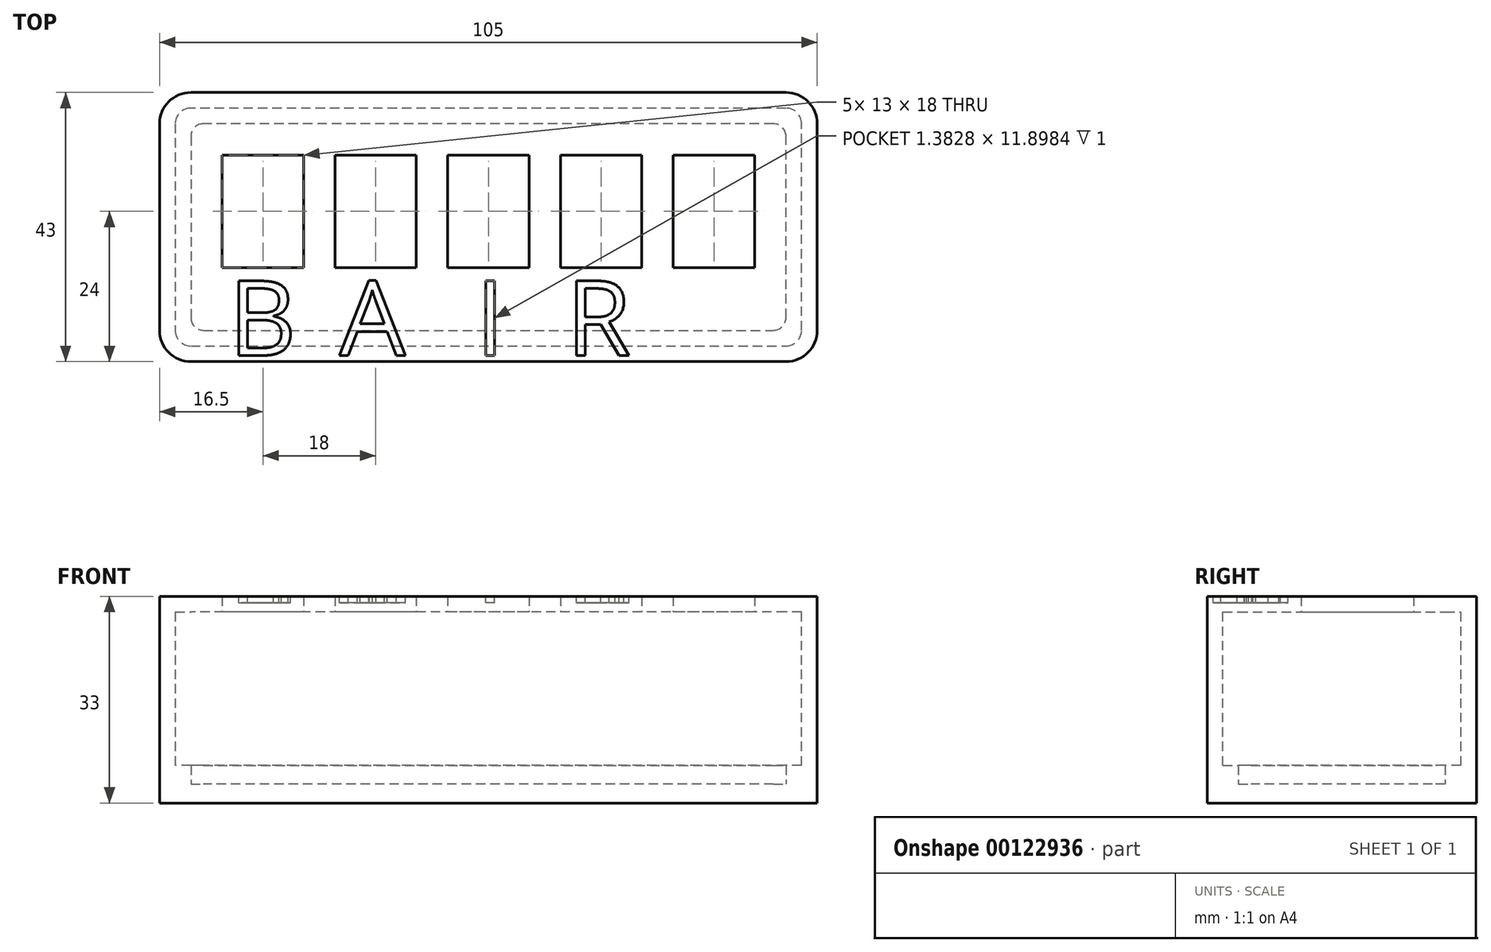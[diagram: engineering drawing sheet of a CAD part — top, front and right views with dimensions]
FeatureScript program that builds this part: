
annotation { "Feature Type Name" : "Feature", "Feature Type Description" : "" }
export const myFeature = defineFeature(function(context is Context, id is Id, definition is map)
    precondition{}
    {
        {
            var Q0;
            Q0=qCreatedBy(makeId("Top.planeOp"),FACE);
            var sketch = newSketch(context, id + "F0", { "sketchPlane" : qUnion([Q0])});
            skLineSegment(sketch, "E0.bottom", {"start": v(-42.5, 33) * mm, "end": v(-29.5, 33) * mm});
            skLineSegment(sketch, "E0.top", {"start": v(-42.5, 15) * mm, "end": v(-29.5, 15) * mm});
            skLineSegment(sketch, "E0.left", {"start": v(-42.5, 33) * mm, "end": v(-42.5, 15) * mm});
            skLineSegment(sketch, "E0.right", {"start": v(-29.5, 33) * mm, "end": v(-29.5, 15) * mm});
            skLineSegment(sketch, "E1.1.0.0", {"start": v(-24.5, 33) * mm, "end": v(-24.5, 15) * mm});
            skLineSegment(sketch, "E1.1.0.1", {"start": v(-24.5, 33) * mm, "end": v(-11.5, 33) * mm});
            skLineSegment(sketch, "E1.1.0.2", {"start": v(-24.5, 15) * mm, "end": v(-11.5, 15) * mm});
            skLineSegment(sketch, "E1.1.0.3", {"start": v(-11.5, 33) * mm, "end": v(-11.5, 15) * mm});
            skLineSegment(sketch, "E1.2.0.0", {"start": v(-6.5, 33) * mm, "end": v(-6.5, 15) * mm});
            skLineSegment(sketch, "E1.2.0.1", {"start": v(-6.5, 33) * mm, "end": v(6.5, 33) * mm});
            skLineSegment(sketch, "E1.2.0.2", {"start": v(-6.5, 15) * mm, "end": v(6.5, 15) * mm});
            skLineSegment(sketch, "E1.2.0.3", {"start": v(6.5, 33) * mm, "end": v(6.5, 15) * mm});
            skLineSegment(sketch, "E1.3.0.0", {"start": v(11.5, 33) * mm, "end": v(11.5, 15) * mm});
            skLineSegment(sketch, "E1.3.0.1", {"start": v(11.5, 33) * mm, "end": v(24.5, 33) * mm});
            skLineSegment(sketch, "E1.3.0.2", {"start": v(11.5, 15) * mm, "end": v(24.5, 15) * mm});
            skLineSegment(sketch, "E1.3.0.3", {"start": v(24.5, 33) * mm, "end": v(24.5, 15) * mm});
            skLineSegment(sketch, "E1.4.0.0", {"start": v(29.5, 33) * mm, "end": v(29.5, 15) * mm});
            skLineSegment(sketch, "E1.4.0.1", {"start": v(29.5, 33) * mm, "end": v(42.5, 33) * mm});
            skLineSegment(sketch, "E1.4.0.2", {"start": v(29.5, 15) * mm, "end": v(42.5, 15) * mm});
            skLineSegment(sketch, "E1.4.0.3", {"start": v(42.5, 33) * mm, "end": v(42.5, 15) * mm});
            skLineSegment(sketch, "E1.direction1", {"start": v(-42.5, 15) * mm, "end": v(-24.5, 15) * mm, "construction": true});
            skLineSegment(sketch, "E2", {"start": v(-52.5, 43) * mm, "end": v(-52.5, 0) * mm});
            skLineSegment(sketch, "E3", {"start": v(-52.5, 0) * mm, "end": v(52.5, 0) * mm});
            skLineSegment(sketch, "E4", {"start": v(52.5, 0) * mm, "end": v(52.5, 43) * mm});
            skLineSegment(sketch, "E5", {"start": v(52.5, 43) * mm, "end": v(-52.5, 43) * mm});
            skSolve(sketch);
        }
        {
            var Q0;
            Q0=makeQuery(id+"F0.imprint","IMPRINT",FACE,{"disambiguationData":[TD([[makeQuery(id+"F0.imprint","IMPRINT",EDGE,{"derivedFrom":sQuery(id+"F0.wireOp",EDGE,"E0.bottom")}),1.0]])]});
            var Q1;
            Q1=makeQuery(id+"F0.imprint","IMPRINT",FACE,{"disambiguationData":[TD([[makeQuery(id+"F0.imprint","IMPRINT",EDGE,{"derivedFrom":sQuery(id+"F0.wireOp",EDGE,"E0.bottom")}),-1.0]])]});
            var Q2;
            Q2=makeQuery(id+"F0.imprint","IMPRINT",FACE,{"disambiguationData":[TD([[makeQuery(id+"F0.imprint","IMPRINT",EDGE,{"derivedFrom":sQuery(id+"F0.wireOp",EDGE,"E1.1.0.0")}),1.0]])]});
            var Q3;
            Q3=makeQuery(id+"F0.imprint","IMPRINT",FACE,{"disambiguationData":[TD([[makeQuery(id+"F0.imprint","IMPRINT",EDGE,{"derivedFrom":sQuery(id+"F0.wireOp",EDGE,"E1.2.0.0")}),1.0]])]});
            var Q4;
            Q4=makeQuery(id+"F0.imprint","IMPRINT",FACE,{"disambiguationData":[TD([[makeQuery(id+"F0.imprint","IMPRINT",EDGE,{"derivedFrom":sQuery(id+"F0.wireOp",EDGE,"E1.3.0.0")}),1.0]])]});
            var Q5;
            Q5=makeQuery(id+"F0.imprint","IMPRINT",FACE,{"disambiguationData":[TD([[makeQuery(id+"F0.imprint","IMPRINT",EDGE,{"derivedFrom":sQuery(id+"F0.wireOp",EDGE,"E1.4.0.0")}),1.0]])]});
            extrude(context, id + "F1", {"entities" : qUnion([Q0, Q1, Q2, Q3, Q4, Q5]), "depth" : 30 * mm});
        }
        {
            var Q0;
            Q0=makeQuery(id+"F1.opExtrude","SWEPT_EDGE",EDGE,{"disambiguationData":[OSD([sQuery(id+"F0.wireOp",EDGE,"E2"),sQuery(id+"F0.wireOp",EDGE,"E3")])]});
            var Q1;
            Q1=makeQuery(id+"F1.opExtrude","SWEPT_EDGE",EDGE,{"disambiguationData":[OSD([sQuery(id+"F0.wireOp",EDGE,"E3"),sQuery(id+"F0.wireOp",EDGE,"E4")])]});
            var Q2;
            Q2=makeQuery(id+"F1.opExtrude","SWEPT_EDGE",EDGE,{"disambiguationData":[OSD([sQuery(id+"F0.wireOp",EDGE,"E4"),sQuery(id+"F0.wireOp",EDGE,"E5")])]});
            var Q3;
            Q3=makeQuery(id+"F1.opExtrude","SWEPT_EDGE",EDGE,{"disambiguationData":[OSD([sQuery(id+"F0.wireOp",EDGE,"E2"),sQuery(id+"F0.wireOp",EDGE,"E5")])]});
            fillet(context, id + "F2", {"entities" : qUnion([Q0, Q1, Q2, Q3]), "radius" : 5 * mm, "tangentPropagation" : true, "allowEdgeOverflow" : false});
        }
        {
            var Q0;
            Q0=makeQuery(id+"F1.opExtrude","CAP_FACE",FACE,{"disambiguationData":[OSD([sQuery(id+"F0.wireOp",EDGE,"E2"),sQuery(id+"F0.wireOp",EDGE,"E3"),sQuery(id+"F0.wireOp",EDGE,"E4"),sQuery(id+"F0.wireOp",EDGE,"E5")])],"isStart":true});
            shell(context, id + "F3", {"entities" : qUnion([Q0]), "thickness" : 2.5 * mm});
        }
        {
            var Q0;
            Q0=makeQuery(id+"F0.imprint","IMPRINT",FACE,{"disambiguationData":[TD([[makeQuery(id+"F0.imprint","IMPRINT",EDGE,{"derivedFrom":sQuery(id+"F0.wireOp",EDGE,"E0.bottom")}),-1.0]])]});
            var Q1;
            Q1=makeQuery(id+"F0.imprint","IMPRINT",FACE,{"disambiguationData":[TD([[makeQuery(id+"F0.imprint","IMPRINT",EDGE,{"derivedFrom":sQuery(id+"F0.wireOp",EDGE,"E1.1.0.0")}),1.0]])]});
            var Q2;
            Q2=makeQuery(id+"F0.imprint","IMPRINT",FACE,{"disambiguationData":[TD([[makeQuery(id+"F0.imprint","IMPRINT",EDGE,{"derivedFrom":sQuery(id+"F0.wireOp",EDGE,"E1.2.0.0")}),1.0]])]});
            var Q3;
            Q3=makeQuery(id+"F0.imprint","IMPRINT",FACE,{"disambiguationData":[TD([[makeQuery(id+"F0.imprint","IMPRINT",EDGE,{"derivedFrom":sQuery(id+"F0.wireOp",EDGE,"E1.3.0.0")}),1.0]])]});
            var Q4;
            Q4=makeQuery(id+"F0.imprint","IMPRINT",FACE,{"disambiguationData":[TD([[makeQuery(id+"F0.imprint","IMPRINT",EDGE,{"derivedFrom":sQuery(id+"F0.wireOp",EDGE,"E1.4.0.0")}),1.0]])]});
            var Q5;
            Q5=makeQuery(id+"F1.opExtrude","CAP_FACE",FACE,{"disambiguationData":[OSD([sQuery(id+"F0.wireOp",EDGE,"E2"),sQuery(id+"F0.wireOp",EDGE,"E3"),sQuery(id+"F0.wireOp",EDGE,"E4"),sQuery(id+"F0.wireOp",EDGE,"E5")])],"isStart":false});
            extrude(context, id + "F4", {"entities" : qUnion([Q0, Q1, Q2, Q3, Q4]), "operationType" : NewBodyOperationType.REMOVE, "endBound" : BoundingType.UP_TO_SURFACE, "endBoundEntityFace" : qUnion([Q5]), "depth" : 25 * mm});
        }
        {
            var Q0;
            Q0=makeQuery(id+"F1.opExtrude","CAP_FACE",FACE,{"disambiguationData":[OSD([sQuery(id+"F0.wireOp",EDGE,"E2"),sQuery(id+"F0.wireOp",EDGE,"E3"),sQuery(id+"F0.wireOp",EDGE,"E4"),sQuery(id+"F0.wireOp",EDGE,"E5")])],"isStart":false});
            var sketch = newSketch(context, id + "F5", { "sketchPlane" : qUnion([Q0])});
            skLineSegment(sketch, "E6.0.0", {"start": v(-42.5, 33) * mm, "end": v(-42.5, 15) * mm});
            skLineSegment(sketch, "E6.0.1", {"start": v(-42.5, 15) * mm, "end": v(-29.5, 15) * mm});
            skLineSegment(sketch, "E6.0.2", {"start": v(-29.5, 15) * mm, "end": v(-29.5, 33) * mm});
            skLineSegment(sketch, "E6.0.3", {"start": v(-29.5, 33) * mm, "end": v(-42.5, 33) * mm});
            skLineSegment(sketch, "E7.0.0", {"start": v(-11.5, 15) * mm, "end": v(-11.5, 33) * mm});
            skLineSegment(sketch, "E7.0.1", {"start": v(-11.5, 33) * mm, "end": v(-24.5, 33) * mm});
            skLineSegment(sketch, "E7.0.2", {"start": v(-24.5, 33) * mm, "end": v(-24.5, 15) * mm});
            skLineSegment(sketch, "E7.0.3", {"start": v(-24.5, 15) * mm, "end": v(-11.5, 15) * mm});
            skLineSegment(sketch, "E8.0.0", {"start": v(6.5, 15) * mm, "end": v(6.5, 33) * mm});
            skLineSegment(sketch, "E8.0.1", {"start": v(6.5, 33) * mm, "end": v(-6.5, 33) * mm});
            skLineSegment(sketch, "E8.0.2", {"start": v(-6.5, 33) * mm, "end": v(-6.5, 15) * mm});
            skLineSegment(sketch, "E8.0.3", {"start": v(-6.5, 15) * mm, "end": v(6.5, 15) * mm});
            skLineSegment(sketch, "E9.0.0", {"start": v(24.5, 15) * mm, "end": v(24.5, 33) * mm});
            skLineSegment(sketch, "E9.0.1", {"start": v(24.5, 33) * mm, "end": v(11.5, 33) * mm});
            skLineSegment(sketch, "E9.0.2", {"start": v(11.5, 33) * mm, "end": v(11.5, 15) * mm});
            skLineSegment(sketch, "E9.0.3", {"start": v(11.5, 15) * mm, "end": v(24.5, 15) * mm});
            skLineSegment(sketch, "E10.0.0", {"start": v(42.5, 15) * mm, "end": v(42.5, 33) * mm});
            skLineSegment(sketch, "E10.0.1", {"start": v(42.5, 33) * mm, "end": v(29.5, 33) * mm});
            skLineSegment(sketch, "E10.0.2", {"start": v(29.5, 33) * mm, "end": v(29.5, 15) * mm});
            skLineSegment(sketch, "E10.0.3", {"start": v(29.5, 15) * mm, "end": v(42.5, 15) * mm});
            skLineSegment(sketch, "E11.0", {"start": v(-47.5, 0) * mm, "end": v(47.5, 0) * mm});
            skText(sketch, "E12", { "text": "B", "fontName": "OpenSans-Regular.ttf"});
            skPoint(sketch, "E13", {"position": v(-36, 15) * mm});
            skLineSegment(sketch, "E14", {"start": v(-36, 15) * mm, "end": v(-36, 0) * mm, "construction": true});
            skLineSegment(sketch, "E15", {"start": v(-18, 15) * mm, "end": v(-18, 0) * mm, "construction": true});
            skLineSegment(sketch, "E16", {"start": v(0, 15) * mm, "end": v(0, 0) * mm, "construction": true});
            skLineSegment(sketch, "E17", {"start": v(18, 15) * mm, "end": v(18, 0) * mm, "construction": true});
            skLineSegment(sketch, "E18", {"start": v(36, 15) * mm, "end": v(36, 0) * mm, "construction": true});
            skLineSegment(sketch, "E19", {"start": v(-36, 13) * mm, "end": v(-18, 13) * mm, "construction": true});
            skText(sketch, "E20", { "text": "A", "fontName": "OpenSans-Regular.ttf"});
            skLineSegment(sketch, "E21", {"start": v(-18, 13) * mm, "end": v(0, 13) * mm, "construction": true});
            skLineSegment(sketch, "E22", {"start": v(0, 13) * mm, "end": v(18, 13) * mm, "construction": true});
            skLineSegment(sketch, "E23", {"start": v(18, 13) * mm, "end": v(36, 13) * mm, "construction": true});
            skText(sketch, "E24", { "text": "I", "fontName": "OpenSans-Regular.ttf"});
            skText(sketch, "E25", { "text": "R", "fontName": "OpenSans-Regular.ttf"});
            const initialGuessF5  = {"E12": [-0.04148, 0.001, 1, 0, 0.012], "E20": [-0.02381, 0.001, 1, 0, 0.012], "E24": [-0.00205, 0.001, 1, 0, 0.012], "E25": [0.01245, 0.001, 1, 0, 0.012]};
            skSetInitialGuess(sketch, initialGuessF5);
            skSolve(sketch);
        }
        {
            var Q0;
            Q0=makeQuery(id+"F5.imprint","IMPRINT",FACE,{"disambiguationData":[TD([[makeQuery(id+"F5.imprint","IMPRINT",EDGE,{"derivedFrom":sQuery(id+"F5.wireOp",EDGE,"E12.sketch_text.stroke-0")}),-1.0]])]});
            var Q1;
            Q1=makeQuery(id+"F5.imprint","IMPRINT",FACE,{"disambiguationData":[TD([[makeQuery(id+"F5.imprint","IMPRINT",EDGE,{"derivedFrom":sQuery(id+"F5.wireOp",EDGE,"E20.sketch_text.stroke-0")}),-1.0]])]});
            var Q2;
            Q2=makeQuery(id+"F5.imprint","IMPRINT",FACE,{"disambiguationData":[TD([[makeQuery(id+"F5.imprint","IMPRINT",EDGE,{"derivedFrom":sQuery(id+"F5.wireOp",EDGE,"E24.sketch_text.stroke-0")}),-1.0]])]});
            var Q3;
            Q3=makeQuery(id+"F5.imprint","IMPRINT",FACE,{"disambiguationData":[TD([[makeQuery(id+"F5.imprint","IMPRINT",EDGE,{"derivedFrom":sQuery(id+"F5.wireOp",EDGE,"E25.sketch_text.stroke-0")}),-1.0]])]});
            extrude(context, id + "F6", {"entities" : qUnion([Q0, Q1, Q2, Q3]), "operationType" : NewBodyOperationType.REMOVE, "oppositeDirection" : true, "depth" : 1 * mm});
        }
        {
            var Q0;
            Q0=makeQuery(id+"F1.opExtrude","CAP_FACE",FACE,{"disambiguationData":[OSD([sQuery(id+"F0.wireOp",EDGE,"E2"),sQuery(id+"F0.wireOp",EDGE,"E3"),sQuery(id+"F0.wireOp",EDGE,"E4"),sQuery(id+"F0.wireOp",EDGE,"E5")])],"isStart":true});
            var sketch = newSketch(context, id + "F7", { "sketchPlane" : qUnion([Q0])});
            skLineSegment(sketch, "E26.0.0", {"start": v(-47.5, -43) * mm, "end": v(47.5, -43) * mm});
            skArc(sketch, "E26.0.1", {"start": v(47.5, -43) * mm, "mid": v(51.04, -41.54) * mm, "end": v(52.5, -38) * mm});
            skLineSegment(sketch, "E26.0.2", {"start": v(52.5, -38) * mm, "end": v(52.5, -5) * mm});
            skArc(sketch, "E26.0.3", {"start": v(52.5, -5) * mm, "mid": v(51.04, -1.46) * mm, "end": v(47.5, 0) * mm});
            skLineSegment(sketch, "E26.0.4", {"start": v(47.5, 0) * mm, "end": v(-47.5, 0) * mm});
            skArc(sketch, "E26.0.5", {"start": v(-47.5, 0) * mm, "mid": v(-51.04, -1.46) * mm, "end": v(-52.5, -5) * mm});
            skLineSegment(sketch, "E26.0.6", {"start": v(-52.5, -5) * mm, "end": v(-52.5, -38) * mm});
            skArc(sketch, "E26.0.7", {"start": v(-52.5, -38) * mm, "mid": v(-51.04, -41.54) * mm, "end": v(-47.5, -43) * mm});
            skLineSegment(sketch, "E27.0", {"start": v(-47.5, -2.5) * mm, "end": v(47.5, -2.5) * mm});
            skArc(sketch, "E28.0", {"start": v(50, -5) * mm, "mid": v(49.27, -3.23) * mm, "end": v(47.5, -2.5) * mm});
            skLineSegment(sketch, "E29.0", {"start": v(50, -5) * mm, "end": v(50, -38) * mm});
            skArc(sketch, "E30.0", {"start": v(47.5, -40.5) * mm, "mid": v(49.27, -39.77) * mm, "end": v(50, -38) * mm});
            skLineSegment(sketch, "E31.0", {"start": v(47.5, -40.5) * mm, "end": v(-47.5, -40.5) * mm});
            skArc(sketch, "E32.0", {"start": v(-50, -38) * mm, "mid": v(-49.27, -39.77) * mm, "end": v(-47.5, -40.5) * mm});
            skLineSegment(sketch, "E33.0", {"start": v(-50, -38) * mm, "end": v(-50, -5) * mm});
            skArc(sketch, "E34.0", {"start": v(-47.5, -2.5) * mm, "mid": v(-49.27, -3.23) * mm, "end": v(-50, -5) * mm});
            skLineSegment(sketch, "E35.0", {"start": v(45.5, -38) * mm, "end": v(-45.5, -38) * mm});
            skLineSegment(sketch, "E35.1", {"start": v(47.5, -7) * mm, "end": v(47.5, -36) * mm});
            skLineSegment(sketch, "E35.2", {"start": v(-45.5, -5) * mm, "end": v(45.5, -5) * mm});
            skLineSegment(sketch, "E35.3", {"start": v(-47.5, -36) * mm, "end": v(-47.5, -7) * mm});
            skArc(sketch, "E36.filletArc", {"start": v(-47.5, -36) * mm, "mid": v(-46.91, -37.41) * mm, "end": v(-45.5, -38) * mm});
            skArc(sketch, "E37.filletArc", {"start": v(45.5, -38) * mm, "mid": v(46.91, -37.41) * mm, "end": v(47.5, -36) * mm});
            skArc(sketch, "E38.filletArc", {"start": v(47.5, -7) * mm, "mid": v(46.91, -5.59) * mm, "end": v(45.5, -5) * mm});
            skArc(sketch, "E39.filletArc", {"start": v(-45.5, -5) * mm, "mid": v(-46.91, -5.59) * mm, "end": v(-47.5, -7) * mm});
            skSolve(sketch);
        }
        {
            var Q0;
            Q0 = qSketchRegion(id + "F7", true);
            var Q1;
            Q1=makeQuery(id+"F7.imprint","IMPRINT",FACE,{"disambiguationData":[TD([[makeQuery(id+"F7.imprint","IMPRINT",EDGE,{"derivedFrom":sQuery(id+"F7.wireOp",EDGE,"E35.0")}),-1.0]])]});
            var Q2;
            Q2=makeQuery(id+"F7.imprint","IMPRINT",FACE,{"disambiguationData":[TD([[makeQuery(id+"F7.imprint","IMPRINT",EDGE,{"derivedFrom":sQuery(id+"F7.wireOp",EDGE,"E27.0")}),-1.0]])]});
            extrude(context, id + "F8", {"entities" : qUnion([Q0, Q1, Q2]), "depth" : 3 * mm});
        }
        {
            var Q0;
            Q0=makeQuery(id+"F7.imprint","IMPRINT",FACE,{"disambiguationData":[TD([[makeQuery(id+"F7.imprint","IMPRINT",EDGE,{"derivedFrom":sQuery(id+"F7.wireOp",EDGE,"E27.0")}),-1.0]])]});
            extrude(context, id + "F9", {"entities" : qUnion([Q0]), "operationType" : NewBodyOperationType.ADD, "oppositeDirection" : true, "depth" : 3 * mm});
        }
    });
